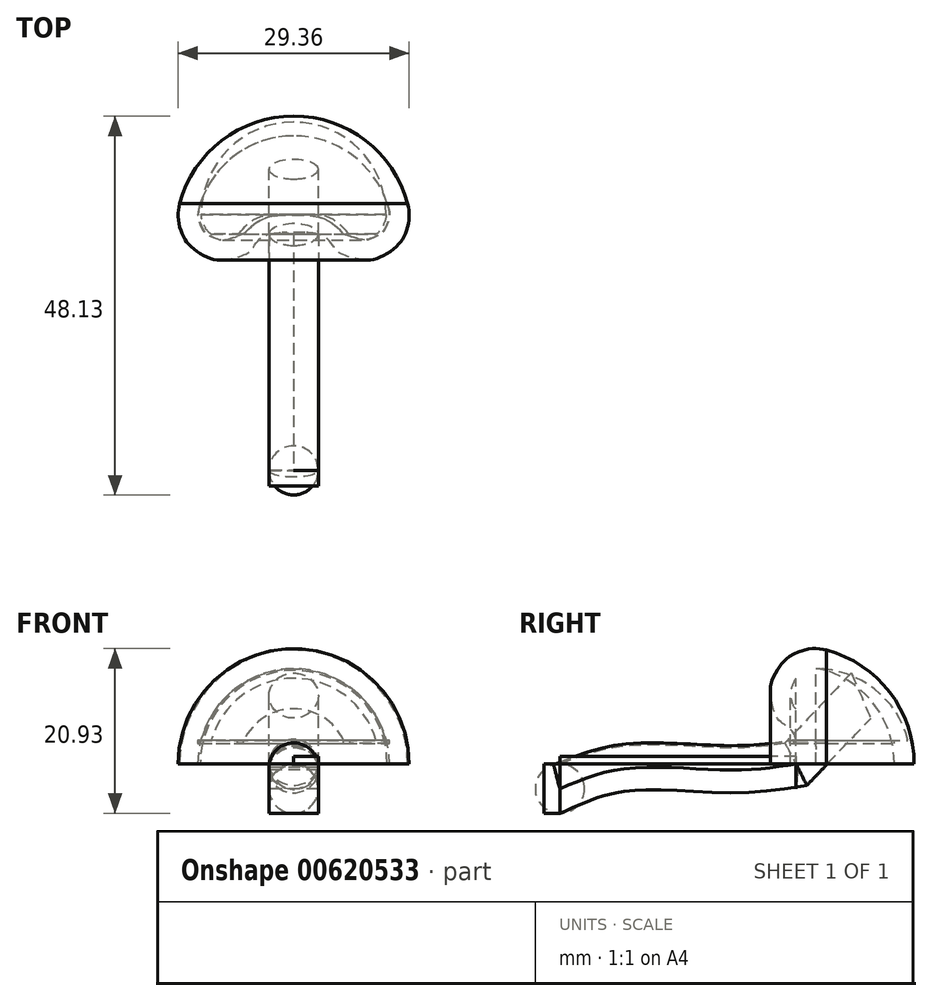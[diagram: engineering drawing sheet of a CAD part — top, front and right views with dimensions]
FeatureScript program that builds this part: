
annotation { "Feature Type Name" : "Feature", "Feature Type Description" : "" }
export const myFeature = defineFeature(function(context is Context, id is Id, definition is map)
    precondition{}
    {
        {
            var Q0;
            Q0=qCreatedBy(makeId("Top.planeOp"),FACE);
            var sketch = newSketch(context, id + "F0", { "sketchPlane" : qUnion([Q0])});
            skArc(sketch, "E0", {"start": v(14.49, 3.88) * mm, "mid": v(0, 15) * mm, "end": v(-14.49, 3.88) * mm});
            skFitSpline(sketch, "E1", {"points": [v(-14.49, 3.88) * mm, v(-14.67, 2.02) * mm, v(-14.1, -0.07) * mm, v(-13.11, -1.5) * mm, v(-10.97, -2.91) * mm, v(-8.92, -3.26) * mm, v(-6.48, -2.67) * mm, v(-5.4, -1.97) * mm, v(-4.1, -0.42) * mm, v(-2.07, 0.17) * mm, v(-1.02, 0.18) * mm, v(0, 0) * mm], "startDerivative": vector(-3.74, -19.6) * mm, "endDerivative": vector(15.18, -3.15) * mm});
            skFitSpline(sketch, "E2.MirrorCS", {"points": [v(14.49, 3.88) * mm, v(14.67, 2.02) * mm, v(14.1, -0.07) * mm, v(13.11, -1.5) * mm, v(10.97, -2.91) * mm, v(8.92, -3.26) * mm, v(6.48, -2.67) * mm, v(5.4, -1.97) * mm, v(4.1, -0.42) * mm, v(2.07, 0.17) * mm, v(1.02, 0.18) * mm, v(0, 0) * mm], "startDerivative": vector(3.74, -19.6) * mm, "endDerivative": vector(-15.18, -3.15) * mm});
            skLineSegment(sketch, "E3.trimOffspring", {"start": v(-3.13, 0) * mm, "end": v(3.13, 0) * mm});
            skLineSegment(sketch, "E4", {"start": v(0, 15) * mm, "end": v(0, 0) * mm});
            skSolve(sketch);
        }
        {
            var Q0;
            {var subQ0=sQuery(id+"F0.wireOp",EDGE,"E3.trimOffspring");var subQ1=sQuery(id+"F0.wireOp",EDGE,"E1");var subQ3=makeQuery(id+"F0.imprint","INTERSECT",VERTEX,{"derivedFrom":[subQ1,subQ0]});Q0=makeQuery(id+"F0.imprint","IMPRINT",FACE,{"disambiguationData":[TD([[makeQuery(id+"F0.imprint","IMPRINT",EDGE,{"disambiguationData":[TD([[subQ3,-1.0]])],"derivedFrom":subQ1}),-1.0]])]});}
            var Q1;
            {var subQ0=sQuery(id+"F0.wireOp",EDGE,"E3.trimOffspring");var subQ1=sQuery(id+"F0.wireOp",EDGE,"E2.MirrorCS");var subQ3=makeQuery(id+"F0.imprint","INTERSECT",VERTEX,{"derivedFrom":[subQ1,subQ0]});Q1=makeQuery(id+"F0.imprint","IMPRINT",FACE,{"disambiguationData":[TD([[makeQuery(id+"F0.imprint","IMPRINT",EDGE,{"disambiguationData":[TD([[subQ3,-1.0]])],"derivedFrom":subQ1}),1.0]])]});}
            var Q2;
            {var subQ3=sQuery(id+"F0.wireOp",EDGE,"E4");Q2=makeQuery(id+"F0.imprint","IMPRINT",FACE,{"disambiguationData":[TD([[makeQuery(id+"F0.imprint","IMPRINT",EDGE,{"derivedFrom":subQ3}),1.0]])]});}
            var Q3;
            Q3=sQuery(id+"F0.wireOp",EDGE,"E4");
            revolve(context, id + "F1", {"entities" : qUnion([Q0, Q1, Q2]), "axis" : qUnion([Q3]), "revolveType" : RevolveType.ONE_DIRECTION, "angle" : 180 * degree});
        }
        {
            var Q0;
            Q0=makeQuery(id+"F1.opRevolve","CAP_FACE",FACE,{"disambiguationData":[OSD([sQuery(id+"F0.wireOp",EDGE,"E0"),sQuery(id+"F0.wireOp",EDGE,"E2.MirrorCS"),sQuery(id+"F0.wireOp",EDGE,"E3.trimOffspring"),sQuery(id+"F0.wireOp",EDGE,"E4")])],"isStart":false});
            var sketch = newSketch(context, id + "F2", { "sketchPlane" : qUnion([Q0])});
            skArc(sketch, "E5", {"start": v(-11.88, -3.88) * mm, "mid": v(0, -12.5) * mm, "end": v(11.88, -3.88) * mm});
            skLineSegment(sketch, "E6", {"start": v(14.49, -3.88) * mm, "end": v(14.68, -2.52) * mm, "construction": true});
            skLineSegment(sketch, "E7", {"start": v(14.68, -2.52) * mm, "end": v(14.3, -0.42) * mm, "construction": true});
            skLineSegment(sketch, "E8", {"start": v(14.3, -0.42) * mm, "end": v(13.11, 1.5) * mm, "construction": true});
            skLineSegment(sketch, "E9", {"start": v(13.11, 1.5) * mm, "end": v(11.35, 2.73) * mm, "construction": true});
            skLineSegment(sketch, "E10", {"start": v(11.35, 2.73) * mm, "end": v(9.25, 3.27) * mm, "construction": true});
            skLineSegment(sketch, "E11", {"start": v(9.25, 3.27) * mm, "end": v(7.87, 3.09) * mm, "construction": true});
            skLineSegment(sketch, "E12", {"start": v(7.87, 3.09) * mm, "end": v(6.48, 2.67) * mm, "construction": true});
            skLineSegment(sketch, "E13", {"start": v(6.48, 2.67) * mm, "end": v(5.56, 2.13) * mm, "construction": true});
            skLineSegment(sketch, "E14", {"start": v(3.13, 0) * mm, "end": v(4.1, 0.43) * mm});
            skLineSegment(sketch, "E15", {"start": v(4.1, 0.43) * mm, "end": v(3.13, 0) * mm, "construction": true});
            skLineSegment(sketch, "E16", {"start": v(14.58, -3.2) * mm, "end": v(12.1, -2.86) * mm, "construction": true});
            skLineSegment(sketch, "E17", {"start": v(14.5, -1.47) * mm, "end": v(12.03, -1.9) * mm, "construction": true});
            skLineSegment(sketch, "E18", {"start": v(13.71, 0.54) * mm, "end": v(11.49, -0.6) * mm, "construction": true});
            skLineSegment(sketch, "E19", {"start": v(12.23, 2.12) * mm, "end": v(10.8, 0.07) * mm, "construction": true});
            skLineSegment(sketch, "E20", {"start": v(10.3, 3) * mm, "end": v(9.67, 0.58) * mm, "construction": true});
            skLineSegment(sketch, "E21", {"start": v(8.56, 3.18) * mm, "end": v(8.9, 0.7) * mm, "construction": true});
            skLineSegment(sketch, "E22", {"start": v(7.18, 2.88) * mm, "end": v(7.9, 0.49) * mm, "construction": true});
            skLineSegment(sketch, "E23", {"start": v(6.02, 2.4) * mm, "end": v(7.27, 0.24) * mm, "construction": true});
            skLineSegment(sketch, "E24", {"start": v(4.1, 0.43) * mm, "end": v(5.56, 2.13) * mm, "construction": true});
            skLineSegment(sketch, "E25", {"start": v(4.83, 1.28) * mm, "end": v(6.73, -0.34) * mm, "construction": true});
            skLineSegment(sketch, "E26", {"start": v(3.62, 0.22) * mm, "end": v(4.62, -2.07) * mm, "construction": true});
            skLineSegment(sketch, "E27", {"start": v(3.13, 0) * mm, "end": v(0, 0) * mm, "construction": true});
            skLineSegment(sketch, "E28", {"start": v(1.56, 0) * mm, "end": v(1.56, -2.5) * mm, "construction": true});
            skFitSpline(sketch, "E29", {"points": [v(11.88, -3.88) * mm, v(12.1, -2.86) * mm, v(12.03, -1.9) * mm, v(11.49, -0.6) * mm, v(10.8, 0.07) * mm, v(9.67, 0.58) * mm, v(8.9, 0.7) * mm, v(7.9, 0.49) * mm, v(7.27, 0.24) * mm, v(6.73, -0.34) * mm, v(4.62, -2.07) * mm, v(1.56, -2.5) * mm, v(0, -2.5) * mm], "startDerivative": vector(3.76, 13.81) * mm, "endDerivative": vector(-15.24, -0.04) * mm});
            skFitSpline(sketch, "E30.MirrorCS", {"points": [v(-11.88, -3.88) * mm, v(-12.1, -2.86) * mm, v(-12.03, -1.9) * mm, v(-11.49, -0.6) * mm, v(-10.8, 0.07) * mm, v(-9.67, 0.58) * mm, v(-8.9, 0.7) * mm, v(-7.9, 0.49) * mm, v(-7.27, 0.24) * mm, v(-6.73, -0.34) * mm, v(-4.62, -2.07) * mm, v(-1.56, -2.5) * mm, v(0, -2.5) * mm], "startDerivative": vector(-3.76, 13.81) * mm, "endDerivative": vector(15.24, -0.04) * mm});
            skLineSegment(sketch, "E31", {"start": v(0, -12.5) * mm, "end": v(0, -2.5) * mm});
            skSolve(sketch);
        }
        {
            var Q0;
            {var subQ0=sQuery(id+"F2.wireOp",EDGE,"E29");Q0=makeQuery(id+"F2.imprint","IMPRINT",FACE,{"disambiguationData":[TD([[makeQuery(id+"F2.imprint","IMPRINT",EDGE,{"derivedFrom":subQ0}),1.0]])]});}
            var Q1;
            Q1=sQuery(id+"F2.wireOp",EDGE,"E31");
            revolve(context, id + "F3", {"operationType" : NewBodyOperationType.REMOVE, "entities" : qUnion([Q0]), "axis" : qUnion([Q1]), "revolveType" : RevolveType.ONE_DIRECTION, "angle" : 180 * degree});
        }
        {
            var Q0;
            Q0=qCreatedBy(makeId("Front.planeOp"),FACE);
            var sketch = newSketch(context, id + "F4", { "sketchPlane" : qUnion([Q0])});
            skLineSegment(sketch, "E32", {"start": v(0, 0) * mm, "end": v(0, 3) * mm});
            skArc(sketch, "E33", {"start": v(14.14, 0) * mm, "mid": v(0, 14.14) * mm, "end": v(-14.14, 0) * mm});
            skLineSegment(sketch, "E34", {"start": v(0, 3) * mm, "end": v(-13.82, 3) * mm});
            skLineSegment(sketch, "E35", {"start": v(-13.82, 3) * mm, "end": v(13.82, 3) * mm});
            skLineSegment(sketch, "E36.bottom", {"start": v(-13.82, 3) * mm, "end": v(12.58, 3) * mm});
            skLineSegment(sketch, "E36.left", {"start": v(-13.82, 3) * mm, "end": v(-13.82, 3.47) * mm});
            skLineSegment(sketch, "E36.right", {"start": v(12.58, 3) * mm, "end": v(12.58, 6.47) * mm});
            skLineSegment(sketch, "E37.left", {"start": v(-13.82, 3.47) * mm, "end": v(-13.82, 3) * mm});
            skLineSegment(sketch, "E37.right", {"start": v(13.82, 3.47) * mm, "end": v(13.82, 3) * mm});
            skLineSegment(sketch, "E38.bottom", {"start": v(-0.5, 3) * mm, "end": v(1.98, 3) * mm});
            skSolve(sketch);
        }
        {
            var Q0;
            {var subQ2=sQuery(id+"F4.wireOp",EDGE,"E36.right");Q0=makeQuery(id+"F4.imprint","IMPRINT",FACE,{"disambiguationData":[TD([[makeQuery(id+"F4.imprint","IMPRINT",EDGE,{"derivedFrom":subQ2}),1.0]])]});}
            extrude(context, id + "F5", {"entities" : qUnion([Q0]), "operationType" : NewBodyOperationType.ADD, "oppositeDirection" : true, "depth" : 2.5 * mm, "offsetDistance" : 25 * mm});
        }
        {
            var Q0;
            Q0=makeQuery(id+"F5.opExtrude","CAP_FACE",FACE,{"disambiguationData":[OSD([sQuery(id+"F4.wireOp",EDGE,"E33"),sQuery(id+"F4.wireOp",EDGE,"E34"),sQuery(id+"F4.wireOp",EDGE,"E35"),sQuery(id+"F4.wireOp",EDGE,"E36.right")])],"isStart":false});
            var sketch = newSketch(context, id + "F6", { "sketchPlane" : qUnion([Q0])});
            skLineSegment(sketch, "E39", {"start": v(0, 3) * mm, "end": v(0, 12.12) * mm});
            skSolve(sketch);
        }
        {
            var Q0;
            {var subQ0=sQuery(id+"F6.wireOp",EDGE,"E39");Q0=makeQuery(id+"F6.imprint","IMPRINT",FACE,{"disambiguationData":[TD([[makeQuery(id+"F6.imprint","IMPRINT",EDGE,{"derivedFrom":subQ0}),-1.0]])]});}
            var Q1;
            Q1=sQuery(id+"F6.wireOp",EDGE,"E39");
            revolve(context, id + "F7", {"entities" : qUnion([Q0]), "axis" : qUnion([Q1]), "revolveType" : RevolveType.ONE_DIRECTION, "oppositeDirection" : true, "angle" : 180 * degree});
        }
        {
            var Q0;
            Q0=makeQuery(id+"F7.opRevolve","SWEPT_FACE",FACE,{"disambiguationData":[OSD([sQuery(id+"F4.wireOp",EDGE,"E34"),sQuery(id+"F4.wireOp",EDGE,"E35")])]});
            var sketch = newSketch(context, id + "F8", { "sketchPlane" : qUnion([Q0])});
            skArc(sketch, "E40.0", {"start": v(11.88, -3.88) * mm, "mid": v(0, -12.5) * mm, "end": v(-11.88, -3.88) * mm});
            skFitSpline(sketch, "E41.0", {"points": [v(-11.88, -3.88) * mm, v(-11.98, -3.53) * mm, v(-12.16, -2.85) * mm, v(-12.1, -1.9) * mm, v(-11.55, -0.54) * mm, v(-10.86, 0.1) * mm, v(-9.67, 0.62) * mm, v(-8.9, 0.78) * mm, v(-7.9, 0.5) * mm, v(-7.21, 0.28) * mm, v(-6.72, -0.4) * mm, v(-4.75, -2.52) * mm, v(-1.6, -2.5) * mm, v(-0.47, -2.5) * mm, v(0, -2.5) * mm]});
            skFitSpline(sketch, "E42.0", {"points": [v(11.88, -3.88) * mm, v(11.98, -3.53) * mm, v(12.16, -2.85) * mm, v(12.1, -1.9) * mm, v(11.55, -0.54) * mm, v(10.86, 0.1) * mm, v(9.67, 0.62) * mm, v(8.9, 0.78) * mm, v(7.9, 0.5) * mm, v(7.21, 0.28) * mm, v(6.72, -0.4) * mm, v(4.75, -2.52) * mm, v(1.6, -2.5) * mm, v(0.47, -2.5) * mm, v(0, -2.5) * mm]});
            skFitSpline(sketch, "E43.0", {"points": [v(-6.34, 0) * mm, v(-6.24, -0.1) * mm, v(-6.05, -0.33) * mm, v(-5.74, -0.65) * mm, v(-5.41, -0.95) * mm, v(-5.07, -1.23) * mm, v(-4.71, -1.48) * mm, v(-4.33, -1.72) * mm, v(-3.93, -1.92) * mm, v(-3.38, -2.13) * mm, v(-2.67, -2.3) * mm, v(-1.78, -2.4) * mm, v(-0.89, -2.45) * mm, v(0, -2.46) * mm, v(0.89, -2.45) * mm, v(1.78, -2.4) * mm, v(2.66, -2.3) * mm, v(3.38, -2.14) * mm, v(3.94, -1.92) * mm, v(4.46, -1.65) * mm, v(4.95, -1.33) * mm, v(5.4, -0.95) * mm, v(5.73, -0.65) * mm, v(6.04, -0.33) * mm, v(6.24, -0.1) * mm, v(6.34, 0) * mm]});
            skFitSpline(sketch, "E44.0.0", {"points": [v(0, -2.5) * mm, v(-0.47, -2.5) * mm, v(-1.6, -2.5) * mm, v(-4.75, -2.52) * mm, v(-6.72, -0.4) * mm, v(-7.21, 0.28) * mm, v(-7.9, 0.5) * mm, v(-8.9, 0.78) * mm, v(-9.67, 0.62) * mm, v(-10.86, 0.1) * mm, v(-11.55, -0.54) * mm, v(-12.1, -1.9) * mm, v(-12.16, -2.85) * mm, v(-11.98, -3.53) * mm, v(-11.88, -3.88) * mm]});
            skFitSpline(sketch, "E44.0.2", {"points": [v(11.88, -3.88) * mm, v(11.98, -3.53) * mm, v(12.16, -2.85) * mm, v(12.1, -1.9) * mm, v(11.55, -0.54) * mm, v(10.86, 0.1) * mm, v(9.67, 0.62) * mm, v(8.9, 0.78) * mm, v(7.9, 0.5) * mm, v(7.21, 0.28) * mm, v(6.72, -0.4) * mm, v(4.75, -2.52) * mm, v(1.6, -2.5) * mm, v(0.47, -2.5) * mm, v(0, -2.5) * mm]});
            skLineSegment(sketch, "E45", {"start": v(-6.34, 0) * mm, "end": v(-8.62, 0.67) * mm});
            skLineSegment(sketch, "E46", {"start": v(6.34, 0) * mm, "end": v(8.8, 0.7) * mm});
            skSolve(sketch);
        }
        {
            var Q0;
            Q0 = qSketchRegion(id + "F8", true);
            extrude(context, id + "F9", {"entities" : qUnion([Q0]), "depth" : 0.4 * mm, "offsetDistance" : 25 * mm});
        }
        {
            var Q0;
            Q0=qCreatedBy(makeId("Top.planeOp"),FACE);
            var sketch = newSketch(context, id + "F10", { "sketchPlane" : qUnion([Q0])});
            skArc(sketch, "E47", {"start": v(-14.49, 3.88) * mm, "mid": v(0, 15) * mm, "end": v(14.49, 3.88) * mm, "construction": true});
            skPoint(sketch, "E48.1.internal.snap0", {"position": v(0, 15) * mm});
            skLineSegment(sketch, "E49", {"start": v(0, 15) * mm, "end": v(0, -30) * mm, "construction": true});
            skLineSegment(sketch, "E50.bottom", {"start": v(0, -30) * mm, "end": v(3.13, -30) * mm});
            skLineSegment(sketch, "E50.top", {"start": v(0, -32) * mm, "end": v(3.13, -32) * mm});
            skLineSegment(sketch, "E50.left", {"start": v(0, -30) * mm, "end": v(0, -32) * mm});
            skLineSegment(sketch, "E50.right", {"start": v(3.13, -30) * mm, "end": v(3.13, -32) * mm});
            skLineSegment(sketch, "E51.MirrorCS", {"start": v(0, -30) * mm, "end": v(-3.13, -30) * mm});
            skLineSegment(sketch, "E52.MirrorCS", {"start": v(0, -32) * mm, "end": v(-3.13, -32) * mm});
            skLineSegment(sketch, "E53.MirrorCS", {"start": v(-3.13, -30) * mm, "end": v(-3.13, -32) * mm});
            skLineSegment(sketch, "E54.bottom", {"start": v(0, 0) * mm, "end": v(3.13, 0) * mm});
            skLineSegment(sketch, "E54.left", {"start": v(0, 0) * mm, "end": v(0, -30) * mm});
            skLineSegment(sketch, "E54.right", {"start": v(3.13, 0) * mm, "end": v(3.13, -30) * mm});
            skSolve(sketch);
        }
        {
            var Q0;
            Q0=makeQuery(id+"F10.imprint","IMPRINT",FACE,{"disambiguationData":[TD([[makeQuery(id+"F10.imprint","IMPRINT",EDGE,{"derivedFrom":sQuery(id+"F10.wireOp",EDGE,"E50.left")}),-1.0]])]});
            var Q1;
            Q1=makeQuery(id+"F10.imprint","IMPRINT",FACE,{"disambiguationData":[TD([[makeQuery(id+"F10.imprint","IMPRINT",EDGE,{"derivedFrom":sQuery(id+"F10.wireOp",EDGE,"E50.top")}),1.0]])]});
            extrude(context, id + "F11", {"entities" : qUnion([Q0, Q1]), "oppositeDirection" : true, "depth" : 6.25 * mm, "offsetDistance" : 25 * mm});
        }
        {
            var Q0;
            Q0=makeQuery(id+"F11.opExtrude","SWEPT_FACE",FACE,{"disambiguationData":[OSD([sQuery(id+"F10.wireOp",EDGE,"E50.bottom"),sQuery(id+"F10.wireOp",EDGE,"E51.MirrorCS")])]});
            var sketch = newSketch(context, id + "F12", { "sketchPlane" : qUnion([Q0])});
            skLineSegment(sketch, "E55", {"start": v(-3.13, -3.13) * mm, "end": v(-3.13, 0) * mm, "construction": true});
            skLineSegment(sketch, "E56", {"start": v(3.13, -0.84) * mm, "end": v(3.13, 0) * mm, "construction": true});
            skLineSegment(sketch, "E57", {"start": v(-3.13, 0) * mm, "end": v(3.13, 0) * mm, "construction": true});
            skLineSegment(sketch, "E58", {"start": v(3.13, 0) * mm, "end": v(-3.13, -6.25) * mm, "construction": true});
            skLineSegment(sketch, "E59", {"start": v(-3.13, -6.25) * mm, "end": v(-3.13, 0) * mm});
            skLineSegment(sketch, "E60", {"start": v(3.13, -6.25) * mm, "end": v(-3.13, 0) * mm, "construction": true});
            skCircle(sketch, "E61", {"center": v(0, -3.13) * mm, "radius": 3.13 * mm});
            skSolve(sketch);
        }
        {
            var Q0;
            Q0=makeQuery(id+"F10.imprint","IMPRINT",FACE,{"disambiguationData":[TD([[makeQuery(id+"F10.imprint","IMPRINT",EDGE,{"derivedFrom":sQuery(id+"F10.wireOp",EDGE,"E54.bottom")}),-1.0]])]});
            extrude(context, id + "F13", {"entities" : qUnion([Q0]), "depth" : 1 * mm, "offsetDistance" : 25 * mm});
        }
        {
            var Q0;
            Q0=makeQuery(id+"F13.opExtrude","SWEPT_FACE",FACE,{"disambiguationData":[OSD([sQuery(id+"F10.wireOp",EDGE,"E54.left")])]});
            var sketch = newSketch(context, id + "F14", { "sketchPlane" : qUnion([Q0])});
            skLineSegment(sketch, "E62.0.0", {"start": v(32, 0) * mm, "end": v(30, 0) * mm, "construction": true});
            skLineSegment(sketch, "E62.0.1", {"start": v(30, 0) * mm, "end": v(30, -6.25) * mm, "construction": true});
            skLineSegment(sketch, "E62.0.2", {"start": v(30, -6.25) * mm, "end": v(32, -6.25) * mm, "construction": true});
            skLineSegment(sketch, "E62.0.3", {"start": v(32, -6.25) * mm, "end": v(32, 0) * mm, "construction": true});
            skFitSpline(sketch, "E63", {"points": [v(30, -3.13) * mm, v(21.56, -0.56) * mm, v(8.18, -0.75) * mm, v(0, 0) * mm], "startDerivative": vector(-24.58, 10.5) * mm, "endDerivative": vector(-24.77, 3.75) * mm});
            skLineSegment(sketch, "E64", {"start": v(0, 0) * mm, "end": v(-8.26, 8.7) * mm});
            skSolve(sketch);
        }
        {
            var Q0;
            {var subQ0=sQuery(id+"F12.wireOp",EDGE,"E61");var subQ5=makeQuery(id+"F12.imprint","INTERSECT",VERTEX,{"derivedFrom":[sQuery(id+"F12.wireOp",EDGE,"E59"),subQ0]});Q0=makeQuery(id+"F12.imprint","IMPRINT",FACE,{"disambiguationData":[TD([[makeQuery(id+"F12.imprint","IMPRINT",EDGE,{"disambiguationData":[TD([[subQ5,1.0]])],"derivedFrom":subQ0}),1.0]])]});}
            var Q1;
            Q1=sQuery(id+"F14.wireOp",EDGE,"E63");
            var Q2;
            Q2=sQuery(id+"F14.wireOp",EDGE,"E64");
            sweep(context, id + "F15", {"profiles" : qUnion([Q0]), "path" : qUnion([Q1, Q2])});
        }
        {
            var Q0;
            {var subQ0=sQuery(id+"F0.wireOp",EDGE,"E3.trimOffspring");var subQ1=sQuery(id+"F0.wireOp",EDGE,"E2.MirrorCS");Q0=makeQuery(id+"F1.opRevolve","SWEPT_FACE",FACE,{"disambiguationData":[OSD([subQ0]),TDD([makeQuery(id+"F0.imprint","IMPRINT",EDGE,{"disambiguationData":[TD([[makeQuery(id+"F0.imprint","INTERSECT",VERTEX,{"derivedFrom":[subQ1,subQ0]}),1.0]])],"derivedFrom":subQ0})])]});}
            var Q1;
            Q1=sQuery(id+"F14.wireOp",EDGE,"E63");
            var Q2;
            Q2=sQuery(id+"F14.wireOp",EDGE,"YPlXaDKz-pfN4-AJQ7-obvI-QgIjoEGbB2oJ");
            sweep(context, id + "F16", {"profiles" : qUnion([Q0]), "path" : qUnion([Q1, Q2])});
        }
        {
            var Q0;
            Q0=makeQuery(id+"F16.opSweep","CAP_FACE",FACE,{"disambiguationData":[OSD([sQuery(id+"F0.wireOp",EDGE,"E3.trimOffspring"),sQuery(id+"F14.wireOp",VERTEX,"E63.start")])],"isStart":false});
            var Q1;
            Q1=makeQuery(id+"F16.opSweep","CAP_EDGE",EDGE,{"disambiguationData":[OSD([sQuery(id+"F0.wireOp",EDGE,"E3.trimOffspring"),sQuery(id+"F14.wireOp",VERTEX,"E63.start")])],"isStart":false});
            revolve(context, id + "F17", {"entities" : qUnion([Q0]), "axis" : qUnion([Q1]), "revolveType" : RevolveType.FULL});
        }
    });
